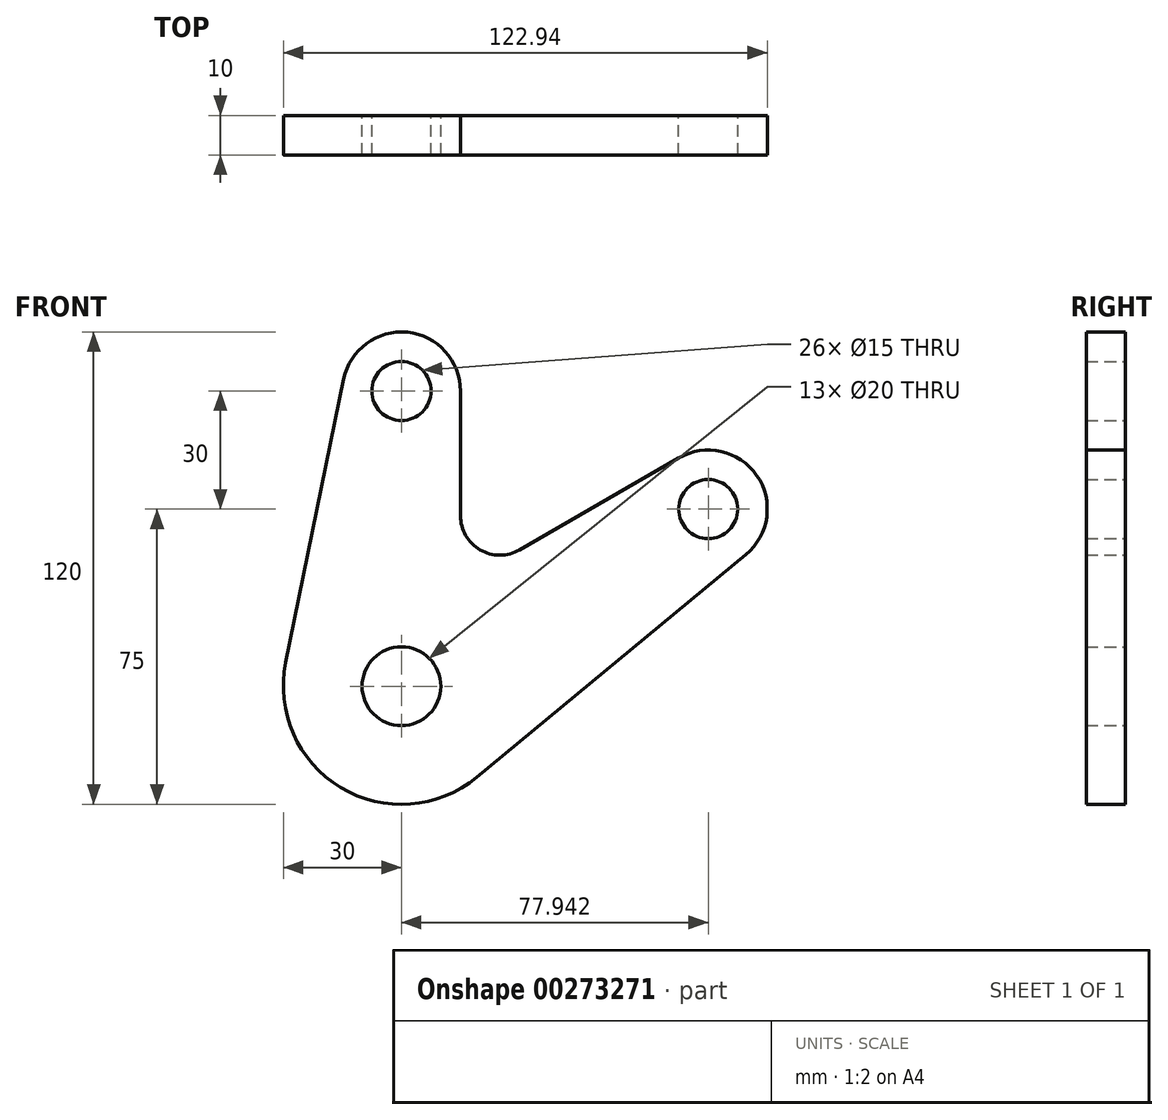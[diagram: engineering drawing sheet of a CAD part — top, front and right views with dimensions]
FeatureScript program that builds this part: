
annotation { "Feature Type Name" : "Feature", "Feature Type Description" : "" }
export const myFeature = defineFeature(function(context is Context, id is Id, definition is map)
    precondition{}
    {
        {
            var Q0;
            Q0=qCreatedBy(makeId("Front.planeOp"),FACE);
            var sketch = newSketch(context, id + "F0", { "sketchPlane" : qUnion([Q0])});
            skCircle(sketch, "E0", {"center": v(0, 0) * mm, "radius": 10 * mm});
            skCircle(sketch, "E1", {"center": v(0, 75) * mm, "radius": 7.5 * mm});
            skCircle(sketch, "E2", {"center": v(77.94, 45) * mm, "radius": 7.5 * mm});
            skLineSegment(sketch, "E3", {"start": v(87.5, 33.44) * mm, "end": v(19.12, -23.12) * mm});
            skLineSegment(sketch, "E4", {"start": v(15, 75) * mm, "end": v(15, 43.3) * mm});
            skArc(sketch, "E5", {"start": v(15, 43.3) * mm, "mid": v(20, 34.64) * mm, "end": v(30, 34.64) * mm});
            skLineSegment(sketch, "E6", {"start": v(30, 34.64) * mm, "end": v(70.44, 58) * mm});
            skArc(sketch, "E7", {"start": v(19.12, -23.12) * mm, "mid": v(-15.44, -25.72) * mm, "end": v(-29.4, 6) * mm});
            skArc(sketch, "E8", {"start": v(15, 75) * mm, "mid": v(1.5, 89.92) * mm, "end": v(-14.7, 78) * mm});
            skLineSegment(sketch, "E9", {"start": v(-14.7, 78) * mm, "end": v(-29.4, 6) * mm});
            skArc(sketch, "E10", {"start": v(70.44, 58) * mm, "mid": v(90.26, 53.56) * mm, "end": v(87.5, 33.44) * mm});
            skLineSegment(sketch, "E11", {"start": v(0, 0) * mm, "end": v(77.94, 45) * mm, "construction": true});
            skLineSegment(sketch, "E12", {"start": v(0, 75) * mm, "end": v(0, 0) * mm, "construction": true});
            skSolve(sketch);
        }
        {
            var Q0;
            Q0=makeQuery(id+"F0.imprint","IMPRINT",FACE,{"disambiguationData":[TD([[makeQuery(id+"F0.imprint","IMPRINT",EDGE,{"derivedFrom":sQuery(id+"F0.wireOp",EDGE,"E0")}),-1.0]])]});
            extrude(context, id + "F1", {"entities" : qUnion([Q0]), "depth" : 10 * mm});
        }
    });
